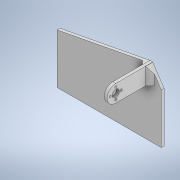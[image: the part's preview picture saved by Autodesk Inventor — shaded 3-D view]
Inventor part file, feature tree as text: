
AUTODESK INVENTOR PART (.ipt)
format: ipt  version: 2020 (Build 240168000, 168)  size: 210,432 bytes
history: native  units: in
note: dims shown in document units (in); Inventor stores cm internally (conversion verified against a paired STEP export)
features: extrude x5, sketch x5, chamfer x2
ambient origin geometry x8: Origin, YZ Plane, XZ Plane, XY Plane, X Axis, Y Axis, Z Axis, Center Point
bodies: Solid1 (feature_tree)
feature tree (12):
  extrude  "Extrusion1"  Depth=1.2in
  extrude  "Extrusion2"  Depth=0.5in
  extrude  "Extrusion3"  Depth=0.1406in
  extrude  "Extrusion4"  Depth=0.2in TaperAngle=0.0deg
  chamfer  "Chamfer1"  Distance=1.2in
  chamfer  "Chamfer2"  Distance=0.2in
  extrude  "Extrusion5"  Depth=0.2in TaperAngle=0.0deg
  sketch  "Sketch1"  dims[d0=1.2in d1=0.77in]
  sketch  "Sketch2"  dims[d2=0.5in d3=0.1406in]
  sketch  "Sketch3"  dims[d4=0.1406in d5=0.1406in]
  sketch  "Sketch4"  dims[d6=0.1406in d7=0.2in d8=0.0in]
  sketch  "Sketch5"  dims[d9=2.4in d10=1.2in d11=0.2in d12=0.2in d13=0.0in d14=6.5in d15=0.2in d16=1.0in d17=3.5in d18=0.0in d19=0.2in d20=0.2in d21=0.0in d22=0.3125in d23=0.125in d24=45.0deg d25=0.3125in d26=0.125in d27=45.0deg d28=0.5in d29=6.7in d30=0.5in d31=0.5in d32=0.5in d33=3.5in d34=0.5in d35=4.0in d36=0.1in d37=0.0in]
